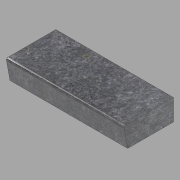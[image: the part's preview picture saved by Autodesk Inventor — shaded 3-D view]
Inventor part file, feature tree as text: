
AUTODESK INVENTOR PART (.ipt)
format: ipt  version: 2022.1 (Build 261234020, 234B)  size: 105,472 bytes
history: native  units: in
note: dims shown in document units (in); Inventor stores cm internally (conversion verified against a paired STEP export)
features: other x3, extrude x1, sketch x1
ambient origin geometry x8: Origin, YZ Plane, XZ Plane, XY Plane, X Axis, Y Axis, Z Axis, Center Point
bodies: Solid1 (feature_tree)
feature tree (5):
  other  "Blocks"
  extrude  "Extrusion1"  Depth=33.375in TaperAngle=0.0deg
  sketch  "Sketch1"  dims[d0=13.0in d1=6.0in d2=13.5in d3=0.5in d4=0.5in d5=33.375in d6=0.0in]
  other  "Profile"
  other  "Profile:1"
